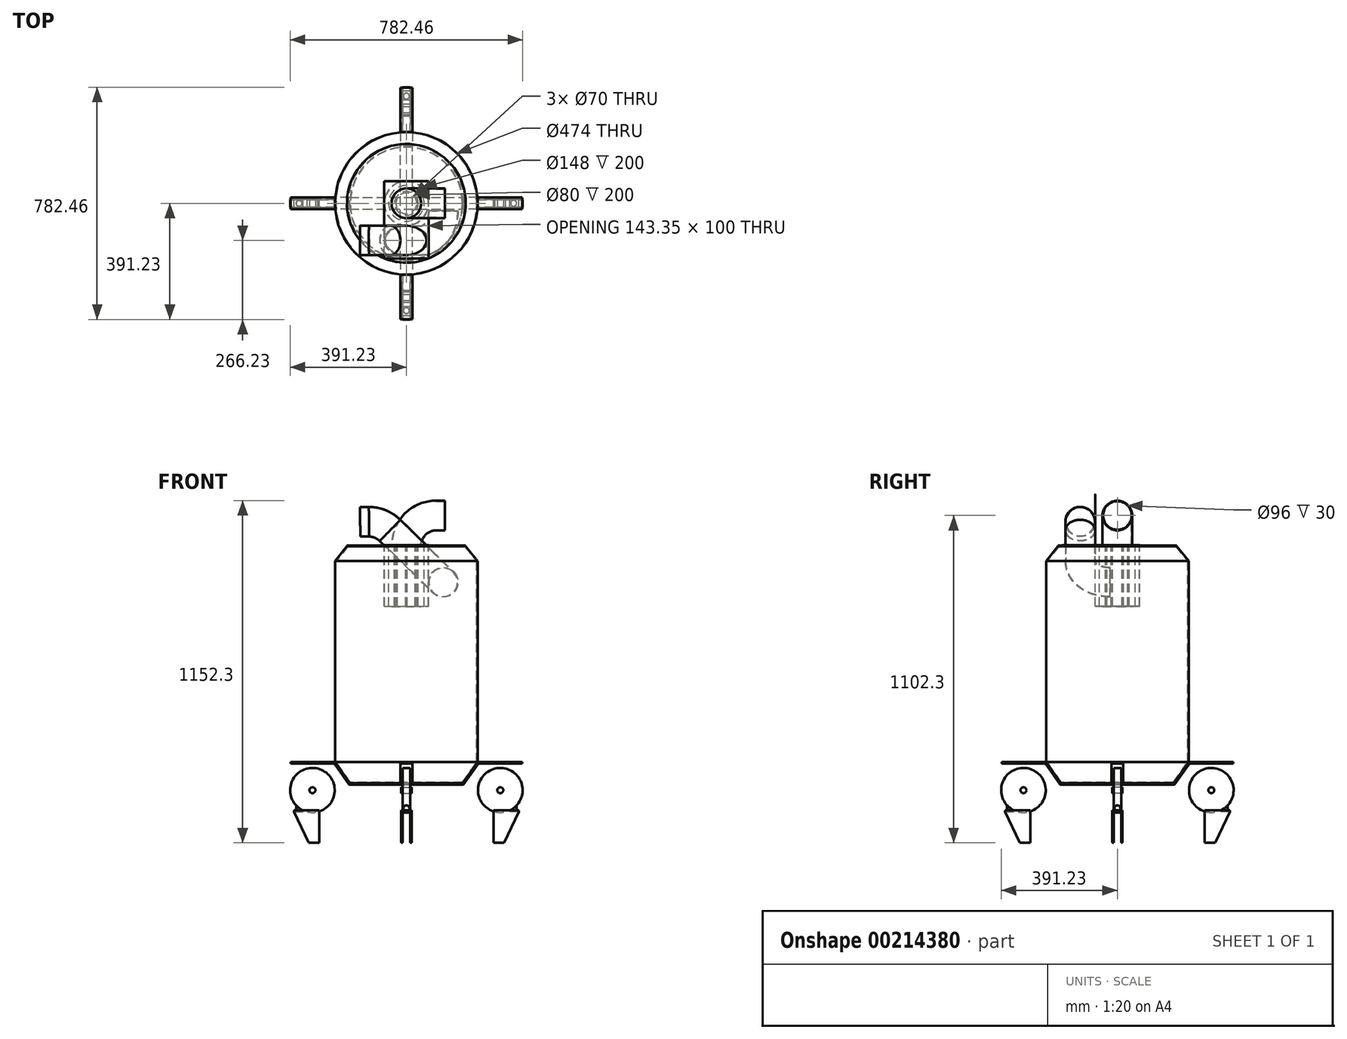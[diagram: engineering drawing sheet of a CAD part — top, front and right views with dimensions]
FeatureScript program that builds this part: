
annotation { "Feature Type Name" : "Feature", "Feature Type Description" : "" }
export const myFeature = defineFeature(function(context is Context, id is Id, definition is map)
    precondition{}
    {
        {
            assignVariable(context, id + "F0", {"name" : "FilterHeight", "anyValue" : 200});
        }
        {
            var Q0;
            Q0=qCreatedBy(makeId("Top.planeOp"),FACE);
            var sketch = newSketch(context, id + "F1", { "sketchPlane" : qUnion([Q0])});
            skCircle(sketch, "E0", {"center": v(0, 0) * mm, "radius": 200 * mm});
            skCircle(sketch, "E1", {"center": v(0, 0) * mm, "radius": 35 * mm});
            skSolve(sketch);
        }
        {
            var Q0;
            Q0 = qSketchRegion(id + "F1", true);
            extrude(context, id + "F2", {"entities" : qUnion([Q0]), "depth" : 3 * mm});
        }
        {
            var Q0;
            Q0=makeQuery(id+"F2.opExtrude","CAP_FACE",FACE,{"disambiguationData":[OSD([sQuery(id+"F1.wireOp",EDGE,"E0"),sQuery(id+"F1.wireOp",EDGE,"E1")])],"isStart":true});
            var sketch = newSketch(context, id + "F3", { "sketchPlane" : qUnion([Q0])});
            skLineSegment(sketch, "E2.bottom", {"start": v(75, -75) * mm, "end": v(-75, -75) * mm});
            skLineSegment(sketch, "E2.top", {"start": v(75, 75) * mm, "end": v(-75, 75) * mm});
            skLineSegment(sketch, "E2.left", {"start": v(75, -75) * mm, "end": v(75, 75) * mm});
            skLineSegment(sketch, "E2.right", {"start": v(-75, -75) * mm, "end": v(-75, 75) * mm});
            skPoint(sketch, "E2.middle", {"position": v(0, 0) * mm});
            skCircle(sketch, "E3.0", {"center": v(0, 0) * mm, "radius": 35 * mm});
            skLineSegment(sketch, "E4.top", {"start": v(75, 185.4) * mm, "end": v(-75, 185.4) * mm});
            skLineSegment(sketch, "E4.left", {"start": v(75, 75) * mm, "end": v(75, 185.4) * mm});
            skLineSegment(sketch, "E4.right", {"start": v(-75, 75) * mm, "end": v(-75, 185.4) * mm});
            skSolve(sketch);
        }
        {
            var Q0;
            Q0 = qSketchRegion(id + "F3", true);
            extrude(context, id + "F4", {"entities" : qUnion([Q0]), "depth" : 1 * mm});
        }
        {
            var Q0;
            Q0=makeQuery(id+"F4.opExtrude","CAP_FACE",FACE,{"disambiguationData":[OSD([sQuery(id+"F3.wireOp",EDGE,"E2.bottom"),sQuery(id+"F3.wireOp",EDGE,"E2.top"),sQuery(id+"F3.wireOp",EDGE,"E2.left"),sQuery(id+"F3.wireOp",EDGE,"E2.right"),sQuery(id+"F3.wireOp",EDGE,"E3.0")])],"isStart":false});
            var sketch = newSketch(context, id + "F5", { "sketchPlane" : qUnion([Q0])});
            skCircle(sketch, "E5", {"center": v(0, 37.5) * mm, "radius": 2.5 * mm});
            skCircle(sketch, "E6.1.0", {"center": v(-32.48, 18.75) * mm, "radius": 2.5 * mm});
            skCircle(sketch, "E6.2.0", {"center": v(-32.48, -18.75) * mm, "radius": 2.5 * mm});
            skCircle(sketch, "E6.3.0", {"center": v(0, -37.5) * mm, "radius": 2.5 * mm});
            skCircle(sketch, "E6.4.0", {"center": v(32.48, -18.75) * mm, "radius": 2.5 * mm});
            skCircle(sketch, "E6.5.0", {"center": v(32.48, 18.75) * mm, "radius": 2.5 * mm});
            skPoint(sketch, "E6.center", {"position": v(0, 0) * mm});
            skSolve(sketch);
        }
        {
            var Q0;
            Q0 = qSketchRegion(id + "F5", true);
            extrude(context, id + "F6", {"entities" : qUnion([Q0]), "depth" : (getVariable(context, 'FilterHeight')) * mm});
        }
        {
            var Q0;
            Q0=makeQuery(id+"F6.opExtrude","CAP_FACE",FACE,{"disambiguationData":[OSD([sQuery(id+"F5.wireOp",EDGE,"E5")])],"isStart":false});
            var sketch = newSketch(context, id + "F7", { "sketchPlane" : qUnion([Q0])});
            skCircle(sketch, "E7", {"center": v(0, 0) * mm, "radius": 40 * mm});
            skSolve(sketch);
        }
        {
            var Q0;
            Q0 = qSketchRegion(id + "F7", true);
            extrude(context, id + "F8", {"entities" : qUnion([Q0]), "depth" : 1 * mm});
        }
        {
            var Q0;
            Q0=makeQuery(id+"F4.opExtrude","CAP_FACE",FACE,{"disambiguationData":[OSD([sQuery(id+"F3.wireOp",EDGE,"E2.bottom"),sQuery(id+"F3.wireOp",EDGE,"E2.top"),sQuery(id+"F3.wireOp",EDGE,"E2.left"),sQuery(id+"F3.wireOp",EDGE,"E2.right"),sQuery(id+"F3.wireOp",EDGE,"E3.0")])],"isStart":false});
            var sketch = newSketch(context, id + "F9", { "sketchPlane" : qUnion([Q0])});
            skCircle(sketch, "E8", {"center": v(0, 0) * mm, "radius": 40 * mm});
            skCircle(sketch, "E9", {"center": v(0, 0) * mm, "radius": 60 * mm});
            skSolve(sketch);
        }
        {
            var Q0;
            Q0 = qSketchRegion(id + "F9", true);
            extrude(context, id + "F10", {"entities" : qUnion([Q0]), "depth" : (getVariable(context, 'FilterHeight')) * mm});
        }
        {
            var Q0;
            Q0=makeQuery(id+"F4.opExtrude","CAP_FACE",FACE,{"disambiguationData":[OSD([sQuery(id+"F3.wireOp",EDGE,"E2.bottom"),sQuery(id+"F3.wireOp",EDGE,"E2.top"),sQuery(id+"F3.wireOp",EDGE,"E2.left"),sQuery(id+"F3.wireOp",EDGE,"E2.right"),sQuery(id+"F3.wireOp",EDGE,"E3.0")])],"isStart":false});
            var sketch = newSketch(context, id + "F11", { "sketchPlane" : qUnion([Q0])});
            skCircle(sketch, "E10", {"center": v(0, 0) * mm, "radius": 75 * mm});
            skCircle(sketch, "E11.0", {"center": v(0, 0) * mm, "radius": 74 * mm});
            skSolve(sketch);
        }
        {
            var Q0;
            Q0 = qSketchRegion(id + "F11", true);
            extrude(context, id + "F12", {"entities" : qUnion([Q0]), "depth" : (getVariable(context, 'FilterHeight')) * mm});
        }
        {
            var Q0;
            Q0=makeQuery(id+"F8.opExtrude","CAP_FACE",FACE,{"disambiguationData":[OSD([sQuery(id+"F7.wireOp",EDGE,"E7")])],"isStart":false});
            var sketch = newSketch(context, id + "F13", { "sketchPlane" : qUnion([Q0])});
            skCircle(sketch, "E12", {"center": v(0, 0) * mm, "radius": 50 * mm});
            skSolve(sketch);
        }
        {
            var Q0;
            Q0 = qSketchRegion(id + "F13", true);
            extrude(context, id + "F14", {"entities" : qUnion([Q0]), "depth" : 1 * mm});
        }
        {
            var Q0;
            Q0=makeQuery(id+"F2.opExtrude","CAP_FACE",FACE,{"disambiguationData":[OSD([sQuery(id+"F1.wireOp",EDGE,"E0"),sQuery(id+"F1.wireOp",EDGE,"E1")])],"isStart":false});
            var sketch = newSketch(context, id + "F15", { "sketchPlane" : qUnion([Q0])});
            skLineSegment(sketch, "E13.bottom", {"start": v(75, -75) * mm, "end": v(-75, -75) * mm});
            skLineSegment(sketch, "E13.top", {"start": v(75, 75) * mm, "end": v(-75, 75) * mm});
            skLineSegment(sketch, "E13.left", {"start": v(75, -75) * mm, "end": v(75, 75) * mm});
            skLineSegment(sketch, "E13.right", {"start": v(-75, -75) * mm, "end": v(-75, 75) * mm});
            skPoint(sketch, "E13.middle", {"position": v(0, 0) * mm});
            skCircle(sketch, "E14.0", {"center": v(0, 0) * mm, "radius": 35 * mm});
            skLineSegment(sketch, "E15.bottom", {"start": v(-75, -75) * mm, "end": v(75, -75) * mm});
            skLineSegment(sketch, "E15.top", {"start": v(-75, -185.4) * mm, "end": v(75, -185.4) * mm});
            skLineSegment(sketch, "E15.left", {"start": v(-75, -75) * mm, "end": v(-75, -185.4) * mm});
            skLineSegment(sketch, "E15.right", {"start": v(75, -75) * mm, "end": v(75, -185.4) * mm});
            skSolve(sketch);
        }
        {
            var Q0;
            Q0 = qSketchRegion(id + "F15", true);
            extrude(context, id + "F16", {"entities" : qUnion([Q0]), "depth" : 1 * mm});
        }
        {
            var Q0;
            Q0=qCreatedBy(makeId("Front.planeOp"),FACE);
            var sketch = newSketch(context, id + "F17", { "sketchPlane" : qUnion([Q0])});
            skArc(sketch, "E16", {"start": v(100, 104) * mm, "mid": v(29.29, 74.71) * mm, "end": v(0, 4) * mm});
            skLineSegment(sketch, "E17", {"start": v(100, 104) * mm, "end": v(130, 104) * mm});
            skLineSegment(sketch, "E18", {"start": v(0, 4) * mm, "end": v(0, -27.41) * mm, "construction": true});
            skSolve(sketch);
        }
        {
            var Q0;
            Q0=makeQuery(id+"F16.opExtrude","CAP_FACE",FACE,{"disambiguationData":[OSD([sQuery(id+"F15.wireOp",EDGE,"E13.bottom"),sQuery(id+"F15.wireOp",EDGE,"E13.top"),sQuery(id+"F15.wireOp",EDGE,"E13.left"),sQuery(id+"F15.wireOp",EDGE,"E13.right"),sQuery(id+"F15.wireOp",EDGE,"E14.0")])],"isStart":false});
            var sketch = newSketch(context, id + "F18", { "sketchPlane" : qUnion([Q0])});
            skCircle(sketch, "E19", {"center": v(0, 0) * mm, "radius": 50 * mm});
            skCircle(sketch, "E20", {"center": v(0, 0) * mm, "radius": 48 * mm});
            skSolve(sketch);
        }
        {
            var Q0;
            Q0=makeQuery(id+"F18.imprint","IMPRINT",FACE,{"disambiguationData":[TD([[makeQuery(id+"F18.imprint","IMPRINT",EDGE,{"derivedFrom":sQuery(id+"F18.wireOp",EDGE,"E19")}),1.0]])]});
            var Q1;
            Q1=sQuery(id+"F17.wireOp",EDGE,"E16");
            var Q2;
            Q2=sQuery(id+"F17.wireOp",EDGE,"E17");
            sweep(context, id + "F19", {"profiles" : qUnion([Q0]), "path" : qUnion([Q1, Q2])});
        }
        {
            var Q0;
            Q0=makeQuery(id+"F2.opExtrude","CAP_FACE",FACE,{"disambiguationData":[OSD([sQuery(id+"F1.wireOp",EDGE,"E0"),sQuery(id+"F1.wireOp",EDGE,"E1")])],"isStart":false});
            var sketch = newSketch(context, id + "F20", { "sketchPlane" : qUnion([Q0])});
            skLineSegment(sketch, "E21", {"start": v(0, 0) * mm, "end": v(0, -207.17) * mm});
            skSolve(sketch);
        }
        {
            var Q0;
            Q0=sQuery(id+"F20.wireOp",EDGE,"E21");
            var Q1;
            Q1=makeQuery(id+"F16.opExtrude","CAP_VERTEX",VERTEX,{"disambiguationData":[OSD([sQuery(id+"F15.wireOp",EDGE,"E13.bottom"),sQuery(id+"F15.wireOp",EDGE,"E13.left")])],"isStart":false});
            cPlane(context, id + "F21", {"entities" : qUnion([Q0, Q1]), "cplaneType" : CPlaneType.LINE_ANGLE, "offset" : 25 * mm, "angle" : 45 * degree, "width" : 150 * mm, "height" : 150 * mm});
        }
        {
            var Q0;
            Q0=qCreatedBy(id+"F21.planeOp",FACE);
            var sketch = newSketch(context, id + "F22", { "sketchPlane" : qUnion([Q0])});
            skCircle(sketch, "E22", {"center": v(125, 0) * mm, "radius": 50 * mm});
            skSolve(sketch);
        }
        {
            var Q0;
            Q0 = qSketchRegion(id + "F22", true);
            extrude(context, id + "F23", {"entities" : qUnion([Q0]), "operationType" : NewBodyOperationType.REMOVE, "endBound" : BoundingType.THROUGH_ALL, "oppositeDirection" : true, "depth" : 25 * mm, "hasSecondDirection" : true, "secondDirectionBound" : SecondDirectionBoundingType.THROUGH_ALL, "secondDirectionOppositeDirection" : false, "secondDirectionDepth" : 25 * mm});
        }
        {
            var Q0;
            Q0=qCreatedBy(id+"F21.planeOp",FACE);
            var sketch = newSketch(context, id + "F24", { "sketchPlane" : qUnion([Q0])});
            skCircle(sketch, "E23.0", {"center": v(125, 0) * mm, "radius": 50 * mm});
            skCircle(sketch, "E24", {"center": v(125, 0) * mm, "radius": 48 * mm});
            skSolve(sketch);
        }
        {
            var Q0;
            Q0 = qSketchRegion(id + "F24", true);
            extrude(context, id + "F25", {"entities" : qUnion([Q0]), "endBound" : BoundingType.SYMMETRIC, "depth" : 150 * mm});
        }
        {
            var Q0;
            Q0=qCreatedBy(makeId("Front.planeOp"),FACE);
            cPlane(context, id + "F26", {"entities" : qUnion([Q0]), "cplaneType" : CPlaneType.OFFSET, "offset" : 125 * mm, "width" : 150 * mm, "height" : 150 * mm});
        }
        {
            var Q0;
            Q0=qCreatedBy(id+"F26.planeOp",FACE);
            var sketch = newSketch(context, id + "F27", { "sketchPlane" : qUnion([Q0])});
            skArc(sketch, "E25", {"start": v(-55.23, 53.78) * mm, "mid": v(-87.5, 75.42) * mm, "end": v(-125.59, 83.01) * mm});
            skLineSegment(sketch, "E26", {"start": v(-125.59, 83.01) * mm, "end": v(-155.59, 83.01) * mm});
            skLineSegment(sketch, "E27.0", {"start": v(-90.12, 17.96) * mm, "end": v(-20.35, 89.6) * mm, "construction": true});
            skLineSegment(sketch, "E28", {"start": v(-125.59, 83.01) * mm, "end": v(-125.59, -8.86) * mm, "construction": true});
            skSolve(sketch);
        }
        {
            var Q0;
            Q0=makeQuery(id+"F25.opExtrude","CAP_FACE",FACE,{"disambiguationData":[OSD([sQuery(id+"F24.wireOp",EDGE,"E23.0"),sQuery(id+"F24.wireOp",EDGE,"E24")])],"isStart":false});
            var sketch = newSketch(context, id + "F28", { "sketchPlane" : qUnion([Q0])});
            skCircle(sketch, "E29.0", {"center": v(125, 0) * mm, "radius": 50 * mm});
            skCircle(sketch, "E30.0", {"center": v(125, 0) * mm, "radius": 48 * mm});
            skSolve(sketch);
        }
        {
            var Q0;
            Q0=makeQuery(id+"F28.imprint","IMPRINT",FACE,{"disambiguationData":[TD([[makeQuery(id+"F28.imprint","IMPRINT",EDGE,{"derivedFrom":sQuery(id+"F28.wireOp",EDGE,"E29.0")}),1.0]])]});
            var Q1;
            Q1=sQuery(id+"F27.wireOp",EDGE,"E25");
            var Q2;
            Q2=sQuery(id+"F27.wireOp",EDGE,"E26");
            sweep(context, id + "F29", {"operationType" : NewBodyOperationType.ADD, "profiles" : qUnion([Q0]), "path" : qUnion([Q1, Q2])});
        }
        {
            var Q0;
            Q0=qCreatedBy(makeId("Right.planeOp"),FACE);
            var sketch = newSketch(context, id + "F30", { "sketchPlane" : qUnion([Q0])});
            skLineSegment(sketch, "E31", {"start": v(-200, 0) * mm, "end": v(-240, -49.57) * mm});
            skLineSegment(sketch, "E32", {"start": v(-240, -49.57) * mm, "end": v(-240, -725.99) * mm});
            skLineSegment(sketch, "E33", {"start": v(-240, -725.99) * mm, "end": v(-190, -797) * mm});
            skLineSegment(sketch, "E34", {"start": v(-190, -797) * mm, "end": v(0, -797) * mm});
            skLineSegment(sketch, "E35", {"start": v(-200, 0) * mm, "end": v(-200, 3) * mm, "construction": true});
            skLineSegment(sketch, "E36.0", {"start": v(-188.44, -794) * mm, "end": v(0, -794) * mm});
            skLineSegment(sketch, "E36.1", {"start": v(-237, -725.04) * mm, "end": v(-188.44, -794) * mm});
            skLineSegment(sketch, "E36.2", {"start": v(-237, -50.63) * mm, "end": v(-237, -725.04) * mm});
            skLineSegment(sketch, "E36.3", {"start": v(-196.15, 0) * mm, "end": v(-237, -50.63) * mm});
            skLineSegment(sketch, "E37", {"start": v(0, -797) * mm, "end": v(0, -794) * mm});
            skLineSegment(sketch, "E38", {"start": v(-196.15, 0) * mm, "end": v(-200, 0) * mm});
            skSolve(sketch);
        }
        {
            var Q0;
            Q0 = qSketchRegion(id + "F30", true);
            var Q1;
            Q1=makeQuery(id+"F12.opExtrude","CAP_EDGE",EDGE,{"disambiguationData":[OSD([sQuery(id+"F11.wireOp",EDGE,"E10")])],"isStart":false});
            revolve(context, id + "F31", {"entities" : qUnion([Q0]), "axis" : qUnion([Q1]), "revolveType" : RevolveType.FULL});
        }
        {
            var Q0;
            Q0=sQuery(id+"F20.wireOp",EDGE,"E21");
            var Q1;
            Q1=makeQuery(id+"F4.opExtrude","CAP_EDGE",EDGE,{"disambiguationData":[OSD([sQuery(id+"F3.wireOp",EDGE,"E2.left"),sQuery(id+"F3.wireOp",EDGE,"E4.left")])],"isStart":true});
            cPlane(context, id + "F32", {"entities" : qUnion([Q0, Q1]), "cplaneType" : CPlaneType.LINE_ANGLE, "offset" : 25 * mm, "angle" : 318 * degree, "width" : 150 * mm, "height" : 150 * mm});
        }
        {
            var Q0;
            Q0=qCreatedBy(id+"F32.planeOp",FACE);
            var sketch = newSketch(context, id + "F33", { "sketchPlane" : qUnion([Q0])});
            skArc(sketch, "E39", {"start": v(73.08, -125) * mm, "mid": v(143.79, -95.71) * mm, "end": v(173.08, -25) * mm});
            skLineSegment(sketch, "E40", {"start": v(73.08, -125) * mm, "end": v(15.66, -125) * mm, "construction": true});
            skLineSegment(sketch, "E41", {"start": v(173.08, -25) * mm, "end": v(173.08, 19.43) * mm, "construction": true});
            skFitSpline(sketch, "E42.0", {"points": [v(72.9, -175) * mm, v(72.9, -175) * mm, v(72.9, -174.36) * mm, v(72.89, -171.5) * mm, v(72.88, -166.84) * mm, v(72.87, -160.58) * mm, v(72.87, -152.96) * mm, v(72.86, -144.26) * mm, v(72.86, -134.82) * mm, v(72.86, -125) * mm, v(72.86, -115.18) * mm, v(72.86, -105.74) * mm, v(72.87, -97.04) * mm, v(72.87, -89.42) * mm, v(72.88, -83.16) * mm, v(72.89, -78.5) * mm, v(72.9, -75.64) * mm, v(72.9, -74.68) * mm, v(72.92, -75.64) * mm, v(72.93, -78.5) * mm, v(72.93, -83.16) * mm, v(72.94, -89.42) * mm, v(72.95, -97.04) * mm, v(72.95, -105.74) * mm, v(72.95, -115.18) * mm, v(72.95, -125) * mm, v(72.95, -134.82) * mm, v(72.95, -144.26) * mm, v(72.95, -152.96) * mm, v(72.94, -160.58) * mm, v(72.93, -166.84) * mm, v(72.93, -171.5) * mm, v(72.92, -174.36) * mm, v(72.91, -175) * mm, v(72.9, -175) * mm, v(72.9, -175) * mm], "construction": true});
            skFitSpline(sketch, "E43.0", {"points": [v(72.9, -175) * mm, v(72.9, -175) * mm, v(72.9, -174.36) * mm, v(72.89, -171.5) * mm, v(72.88, -166.84) * mm, v(72.87, -160.58) * mm, v(72.87, -152.96) * mm, v(72.86, -144.26) * mm, v(72.86, -134.82) * mm, v(72.86, -125) * mm, v(72.86, -115.18) * mm, v(72.86, -105.74) * mm, v(72.87, -97.04) * mm, v(72.87, -89.42) * mm, v(72.88, -83.16) * mm, v(72.89, -78.5) * mm, v(72.9, -75.64) * mm, v(72.9, -74.68) * mm, v(72.92, -75.64) * mm, v(72.93, -78.5) * mm, v(72.93, -83.16) * mm, v(72.94, -89.42) * mm, v(72.95, -97.04) * mm, v(72.95, -105.74) * mm, v(72.95, -115.18) * mm, v(72.95, -125) * mm, v(72.95, -134.82) * mm, v(72.95, -144.26) * mm, v(72.95, -152.96) * mm, v(72.94, -160.58) * mm, v(72.93, -166.84) * mm, v(72.93, -171.5) * mm, v(72.92, -174.36) * mm, v(72.91, -175) * mm, v(72.9, -175) * mm, v(72.9, -175) * mm], "construction": true});
            skLineSegment(sketch, "E44", {"start": v(73.08, -54.23) * mm, "end": v(73.08, -228.17) * mm, "construction": true});
            skLineSegment(sketch, "E45", {"start": v(-77.1, -75) * mm, "end": v(72.9, -75) * mm, "construction": true});
            skLineSegment(sketch, "E46", {"start": v(72.9, -175) * mm, "end": v(-77.1, -175) * mm, "construction": true});
            skSolve(sketch);
        }
        {
            var Q0;
            Q0=makeQuery(id+"F25.opExtrude","CAP_FACE",FACE,{"disambiguationData":[OSD([sQuery(id+"F24.wireOp",EDGE,"E23.0"),sQuery(id+"F24.wireOp",EDGE,"E24")])],"isStart":true});
            var sketch = newSketch(context, id + "F34", { "sketchPlane" : qUnion([Q0])});
            skCircle(sketch, "E47.0", {"center": v(-125, 0) * mm, "radius": 48 * mm});
            skCircle(sketch, "E48.0", {"center": v(-125, 0) * mm, "radius": 50 * mm});
            skSolve(sketch);
        }
        {
            var Q0;
            Q0=makeQuery(id+"F34.imprint","IMPRINT",FACE,{"disambiguationData":[TD([[makeQuery(id+"F34.imprint","IMPRINT",EDGE,{"derivedFrom":sQuery(id+"F34.wireOp",EDGE,"E47.0")}),1.0]])]});
            var Q1;
            Q1=sQuery(id+"F33.wireOp",EDGE,"E39");
            sweep(context, id + "F35", {"operationType" : NewBodyOperationType.ADD, "profiles" : qUnion([Q0]), "path" : qUnion([Q1])});
        }
        {
            var Q0;
            Q0=qCreatedBy(makeId("Front.planeOp"),FACE);
            var sketch = newSketch(context, id + "F36", { "sketchPlane" : qUnion([Q0])});
            skLineSegment(sketch, "E49.0", {"start": v(-190, -797) * mm, "end": v(190, -797) * mm});
            skLineSegment(sketch, "E50", {"start": v(-96.84, -929.3) * mm, "end": v(-240, -725.99) * mm});
            skLineSegment(sketch, "E51", {"start": v(240, -725.99) * mm, "end": v(96.84, -929.3) * mm});
            skLineSegment(sketch, "E52", {"start": v(240, -725.99) * mm, "end": v(390, -725.99) * mm});
            skLineSegment(sketch, "E53", {"start": v(-240, -725.99) * mm, "end": v(-390, -725.99) * mm});
            skLineSegment(sketch, "E54.0", {"start": v(242.6, -730.99) * mm, "end": v(390, -730.99) * mm});
            skLineSegment(sketch, "E54.1", {"start": v(-242.6, -730.99) * mm, "end": v(-390, -730.99) * mm});
            skLineSegment(sketch, "E54.2", {"start": v(-192.6, -802) * mm, "end": v(-242.6, -730.99) * mm});
            skLineSegment(sketch, "E54.3", {"start": v(-192.6, -802) * mm, "end": v(192.6, -802) * mm});
            skLineSegment(sketch, "E54.4", {"start": v(242.6, -730.99) * mm, "end": v(192.6, -802) * mm});
            skLineSegment(sketch, "E55", {"start": v(-390, -730.99) * mm, "end": v(-390, -725.99) * mm});
            skLineSegment(sketch, "E56", {"start": v(390, -730.99) * mm, "end": v(390, -725.99) * mm});
            skSolve(sketch);
        }
        {
            var Q0;
            Q0 = qSketchRegion(id + "F36", true);
            extrude(context, id + "F37", {"entities" : qUnion([Q0]), "endBound" : BoundingType.SYMMETRIC, "depth" : 40 * mm});
        }
        {
            var Q0;
            Q0=makeQuery(id+"F37.opExtrude","SWEPT_BODY",BODY,{"disambiguationData":[OSD([sQuery(id+"F36.wireOp",EDGE,"E49.0"),sQuery(id+"F36.wireOp",EDGE,"E50"),sQuery(id+"F36.wireOp",EDGE,"E51"),sQuery(id+"F36.wireOp",EDGE,"E52"),sQuery(id+"F36.wireOp",EDGE,"E53"),sQuery(id+"F36.wireOp",EDGE,"E54.0"),sQuery(id+"F36.wireOp",EDGE,"E54.1"),sQuery(id+"F36.wireOp",EDGE,"E54.2"),sQuery(id+"F36.wireOp",EDGE,"E54.3"),sQuery(id+"F36.wireOp",EDGE,"E54.4"),sQuery(id+"F36.wireOp",EDGE,"E55"),sQuery(id+"F36.wireOp",EDGE,"E56")])]});
            var Q1;
            Q1=makeQuery(id+"F31.opRevolve","SWEPT_EDGE",EDGE,{"disambiguationData":[OSD([sQuery(id+"F30.wireOp",EDGE,"E33"),sQuery(id+"F30.wireOp",EDGE,"E34")])]});
            transform(context, id + "F38", {"entities" : qUnion([Q0]), "transformType" : TransformType.ROTATION, "transformAxis" : qUnion([Q1]), "angle" : 90 * degree, "makeCopy" : true});
        }
        {
            var Q0;
            Q0=qCreatedBy(makeId("Front.planeOp"),FACE);
            var sketch = newSketch(context, id + "F39", { "sketchPlane" : qUnion([Q0])});
            skCircle(sketch, "E57", {"center": v(-316.23, -820.99) * mm, "radius": 75 * mm});
            skSolve(sketch);
        }
        {
            var Q0;
            Q0 = qSketchRegion(id + "F39", true);
            extrude(context, id + "F40", {"entities" : qUnion([Q0]), "endBound" : BoundingType.SYMMETRIC, "depth" : 25 * mm});
        }
        {
            var Q0;
            Q0=makeQuery(id+"F40.opExtrude","CAP_FACE",FACE,{"disambiguationData":[OSD([sQuery(id+"F39.wireOp",EDGE,"E57")])],"isStart":false});
            var sketch = newSketch(context, id + "F41", { "sketchPlane" : qUnion([Q0])});
            skLineSegment(sketch, "E58", {"start": v(-293.27, -893.88) * mm, "end": v(-293.27, -998.3) * mm});
            skLineSegment(sketch, "E59", {"start": v(-293.27, -998.3) * mm, "end": v(-328.82, -998.3) * mm});
            skLineSegment(sketch, "E60", {"start": v(-328.82, -998.3) * mm, "end": v(-378.43, -893.88) * mm});
            skLineSegment(sketch, "E61", {"start": v(-378.43, -893.88) * mm, "end": v(-293.27, -893.88) * mm});
            skSolve(sketch);
        }
        {
            var Q0;
            Q0 = qSketchRegion(id + "F41", true);
            extrude(context, id + "F42", {"entities" : qUnion([Q0]), "depth" : 5 * mm});
        }
        {
            var Q0;
            Q0=makeQuery(id+"F42.opExtrude","SWEPT_BODY",BODY,{"disambiguationData":[OSD([sQuery(id+"F41.wireOp",EDGE,"E58"),sQuery(id+"F41.wireOp",EDGE,"E59"),sQuery(id+"F41.wireOp",EDGE,"E60"),sQuery(id+"F41.wireOp",EDGE,"E61")])]});
            var Q1;
            Q1=qCreatedBy(makeId("Front.planeOp"),FACE);
            mirror(context, id + "F43", {"entities" : qUnion([Q0]), "mirrorPlane" : qUnion([Q1])});
        }
        {
            var Q0;
            Q0=makeQuery(id+"F42.opExtrude","SWEPT_FACE",FACE,{"disambiguationData":[OSD([sQuery(id+"F41.wireOp",EDGE,"E61")])]});
            var sketch = newSketch(context, id + "F44", { "sketchPlane" : qUnion([Q0])});
            skLineSegment(sketch, "E62.bottom", {"start": v(-378.43, -17.5) * mm, "end": v(-293.27, -17.5) * mm});
            skLineSegment(sketch, "E62.top", {"start": v(-378.43, 17.5) * mm, "end": v(-293.27, 17.5) * mm});
            skLineSegment(sketch, "E62.left", {"start": v(-378.43, -17.5) * mm, "end": v(-378.43, 17.5) * mm});
            skLineSegment(sketch, "E62.right", {"start": v(-293.27, -17.5) * mm, "end": v(-293.27, 17.5) * mm});
            skSolve(sketch);
        }
        {
            var Q0;
            Q0 = qSketchRegion(id + "F44", true);
            extrude(context, id + "F45", {"entities" : qUnion([Q0]), "operationType" : NewBodyOperationType.ADD, "depth" : 5 * mm});
        }
        {
            var Q0;
            Q0=makeQuery(id+"F45.opExtrude","CAP_FACE",FACE,{"disambiguationData":[OSD([sQuery(id+"F44.wireOp",EDGE,"E62.bottom"),sQuery(id+"F44.wireOp",EDGE,"E62.top"),sQuery(id+"F44.wireOp",EDGE,"E62.left"),sQuery(id+"F44.wireOp",EDGE,"E62.right")])],"isStart":false});
            var sketch = newSketch(context, id + "F46", { "sketchPlane" : qUnion([Q0])});
            skCircle(sketch, "E63", {"center": v(-361.28, 0) * mm, "radius": 10 * mm});
            skSolve(sketch);
        }
        {
            var Q0;
            Q0 = qSketchRegion(id + "F46", true);
            extrude(context, id + "F47", {"entities" : qUnion([Q0]), "operationType" : NewBodyOperationType.ADD, "depth" : 25 * mm});
        }
        {
            var Q0;
            Q0=makeQuery(id+"F45.boolean.opBoolean","MERGE",FACE,{"derivedFrom":[makeQuery(id+"F42.opExtrude","CAP_FACE",FACE,{"disambiguationData":[OSD([sQuery(id+"F41.wireOp",EDGE,"E58"),sQuery(id+"F41.wireOp",EDGE,"E59"),sQuery(id+"F41.wireOp",EDGE,"E60"),sQuery(id+"F41.wireOp",EDGE,"E61")])],"isStart":false}),makeQuery(id+"F45.opExtrude","SWEPT_FACE",FACE,{"disambiguationData":[OSD([sQuery(id+"F44.wireOp",EDGE,"E62.bottom")])]})]});
            var sketch = newSketch(context, id + "F48", { "sketchPlane" : qUnion([Q0])});
            skCircle(sketch, "E64", {"center": v(-316.23, -820.99) * mm, "radius": 10 * mm});
            skSolve(sketch);
        }
        {
            var Q0;
            Q0 = qSketchRegion(id + "F48", true);
            var Q1;
            Q1=makeQuery(id+"F45.boolean.opBoolean","MERGE",FACE,{"derivedFrom":[makeQuery(id+"F43.opPattern","COPY",FACE,{"derivedFrom":makeQuery(id+"F42.opExtrude","CAP_FACE",FACE,{"disambiguationData":[OSD([sQuery(id+"F41.wireOp",EDGE,"E58"),sQuery(id+"F41.wireOp",EDGE,"E59"),sQuery(id+"F41.wireOp",EDGE,"E60"),sQuery(id+"F41.wireOp",EDGE,"E61")])],"isStart":false}),"instanceName":"1"}),makeQuery(id+"F45.opExtrude","SWEPT_FACE",FACE,{"disambiguationData":[OSD([sQuery(id+"F44.wireOp",EDGE,"E62.top")])]})]});
            extrude(context, id + "F49", {"entities" : qUnion([Q0]), "endBound" : BoundingType.UP_TO_SURFACE, "oppositeDirection" : true, "endBoundEntityFace" : qUnion([Q1]), "depth" : 25 * mm});
        }
        {
            var Q0;
            Q0=makeQuery(id+"F42.opExtrude","SWEPT_BODY",BODY,{"disambiguationData":[OSD([sQuery(id+"F41.wireOp",EDGE,"E58"),sQuery(id+"F41.wireOp",EDGE,"E59"),sQuery(id+"F41.wireOp",EDGE,"E60"),sQuery(id+"F41.wireOp",EDGE,"E61")])]});
            var Q1;
            Q1=makeQuery(id+"F49.opExtrude","SWEPT_BODY",BODY,{"disambiguationData":[OSD([sQuery(id+"F48.wireOp",EDGE,"E64")])]});
            var Q2;
            Q2=makeQuery(id+"F40.opExtrude","SWEPT_BODY",BODY,{"disambiguationData":[OSD([sQuery(id+"F39.wireOp",EDGE,"E57")])]});
            var Q3;
            Q3=qCreatedBy(makeId("Right.planeOp"),FACE);
            mirror(context, id + "F50", {"entities" : qUnion([Q0, Q1, Q2]), "mirrorPlane" : qUnion([Q3])});
        }
        {
            var Q0;
            Q0=makeQuery(id+"F40.opExtrude","SWEPT_BODY",BODY,{"disambiguationData":[OSD([sQuery(id+"F39.wireOp",EDGE,"E57")])]});
            var Q1;
            Q1=makeQuery(id+"F49.opExtrude","SWEPT_BODY",BODY,{"disambiguationData":[OSD([sQuery(id+"F48.wireOp",EDGE,"E64")])]});
            var Q2;
            Q2=makeQuery(id+"F42.opExtrude","SWEPT_BODY",BODY,{"disambiguationData":[OSD([sQuery(id+"F41.wireOp",EDGE,"E58"),sQuery(id+"F41.wireOp",EDGE,"E59"),sQuery(id+"F41.wireOp",EDGE,"E60"),sQuery(id+"F41.wireOp",EDGE,"E61")])]});
            var Q3;
            Q3=makeQuery(id+"F31.opRevolve","SWEPT_EDGE",EDGE,{"disambiguationData":[OSD([sQuery(id+"F30.wireOp",EDGE,"E33"),sQuery(id+"F30.wireOp",EDGE,"E34")])]});
            transform(context, id + "F51", {"entities" : qUnion([Q0, Q1, Q2]), "transformType" : TransformType.ROTATION, "transformAxis" : qUnion([Q3]), "angle" : 90 * degree, "makeCopy" : true});
        }
        {
            var Q0;
            Q0=makeQuery(id+"F51.opPattern","COPY",BODY,{"derivedFrom":makeQuery(id+"F40.opExtrude","SWEPT_BODY",BODY,{"disambiguationData":[OSD([sQuery(id+"F39.wireOp",EDGE,"E57")])]}),"instanceName":"1"});
            var Q1;
            Q1=makeQuery(id+"F51.opPattern","COPY",BODY,{"derivedFrom":makeQuery(id+"F49.opExtrude","SWEPT_BODY",BODY,{"disambiguationData":[OSD([sQuery(id+"F48.wireOp",EDGE,"E64")])]}),"instanceName":"1"});
            var Q2;
            Q2=makeQuery(id+"F51.opPattern","COPY",BODY,{"derivedFrom":makeQuery(id+"F42.opExtrude","SWEPT_BODY",BODY,{"disambiguationData":[OSD([sQuery(id+"F41.wireOp",EDGE,"E58"),sQuery(id+"F41.wireOp",EDGE,"E59"),sQuery(id+"F41.wireOp",EDGE,"E60"),sQuery(id+"F41.wireOp",EDGE,"E61")])]}),"instanceName":"1"});
            var Q3;
            Q3=qCreatedBy(makeId("Front.planeOp"),FACE);
            mirror(context, id + "F52", {"entities" : qUnion([Q0, Q1, Q2]), "mirrorPlane" : qUnion([Q3])});
        }
    });
